# Revit family: plfy-p22_140lmg9_50Hz
name_source: partatom
category: 機械設備
units: mm (PartAtom-declared; Revit-internal decimal feet)

## family parameters
OmniClass タイトル = Split System Air Conditioning Units
OmniClass 番号 = 23.75.10.24.21.27.27
パーツ タイプ = 標準
ロード時にボイドで切り取り = いいえ
丸型コネクタ寸法 = 直径を使用
作業面ベース = いいえ
共有 = いいえ
常に垂直 = はい
部屋計算ポイント = はい

## types (10) — shared parameters
Clearance Back = 500  [stored 1.64042 ft]
Clearance Bottom = 1000  [stored 3.28084 ft]
Clearance Front = 500  [stored 1.64042 ft]
Clearance Left = 1500  [stored 4.92126 ft]
Clearance Right = 1500  [stored 4.92126 ft]
IfcExportAs = IfcUnitaryEquipmentType
IfcExportType = AIRCONDITIONINGUNIT
OmniClassCode = 23-751024212727
URL = https://www.mitsubishielectric.co.jp
Uniclass2015Code = Pr_70_65_03_84
Uniclass2015Title = Split coil remote air cooled condensing units
Uniclass2015Version = Systems v1.9
Width = 650  [stored 2.13255 ft]
ケーブルサイズ = 2 mm
サービススペース = はい
ドレン管径 = 32 mm
ドレン管高さ = 297  [stored 0.974409 ft]
パネルマテリアル = <カテゴリ別>
仕様書バージョン = Version1.0
企業コード = 108420
冷媒ガス管高さ = 235  [stored 0.770997 ft]
冷媒液管高さ = 235  [stored 0.770997 ft]
冷媒管径 = 100 mm
冷媒高低圧ガス管径 = 0 mm
分類コード = 50053003221020
加湿給水管径 = 0 mm
参照している仕様書等のバージョン = 公共建築工事標準仕様書（機械設備工事編）平成31年度版
吊りボルト_H = 167  [stored 0.5479 ft]
吊り位置X = 574  [stored 1.8832 ft]
周波数 = 50 Hz
呼称 = 室内機_カセット形(2方向吹出形)
形式 = カセット形（2方向吹出形）
推奨ブレーカー容量 = 15 A
本体マテリアル = <カテゴリ別>
極数 = 3
機外静圧 = 0.0 Pa
法定耐用年数 = 15
消費電力_加湿器 = 0.00 kW
消費電力_電気ヒーター = 0.00 kW
発停方法 = 付属スイッチ
相 = 1
相_電気ヒーター = 1
積算_科目 = 1 空気調和設備
符号 = ACP_CK2
製品リリース年月 = 2022年9月15日
製品出荷対象 = 国内
製造元 = 三菱電機株式会社
設置方法 = カセット形
設計冷房能力 = 0 kW
設計冷房能力_顕熱 = 0 kW
設計暖房能力 = 0.00 kW
説明 = ビル用マルチエアコン 天井カセット形(2方向吹出)室内機
負荷分類 = 3_ファン類
運転質量 = 0.00 kg
電圧 = 200 V
電圧_電気ヒーター = 0 V
zero-valued in all types: 有効加湿量, 電源_H

## per-type parameters (varying)
- PLFY-P22LMG9: Clearance Top=357  [stored 1.17126 ft]; Depth=770  [stored 2.52625 ft]; Height=290  [stored 0.951444 ft]; MAX風量=570.0 m³/h; MID風量=510.0 m³/h; MID風量2=450.0 m³/h; MIN風量=390.0 m³/h; S_H=364  [stored 1.19423 ft]; 冷媒ガス管径=13 mm; 冷媒ガス管長さ=78  [stored 0.255906 ft]; 冷媒液管径=6 mm; 冷媒液管長さ=67  [stored 0.219816 ft]; 冷媒管径符号=Ac; 冷房能力=2.2 kW; 吊り位置Y=824  [stored 2.70341 ft]; 暖房能力=2.50 kW; 消費電力=0.03 kW; 消費電力_冷房=0.03 kW; 消費電力_暖房=0.03 kW; 製品質量=20.00 kg; 質量=24.00 kg; 電動機出力_送風機=0.05 kW; 音響パワーレベル(dB)=53; 音響パワーレベル（中1）(dB)=52; 音響パワーレベル（中2）(dB)=51; 音響パワーレベル（弱）(dB)=49; 風量=570.0 m³/h; 風量（m3／min）=9.5; 風量（中1）（m3／min）=8.5; 風量（中2）（m3／min）=7.5; 風量（弱）（m3／min）=6.5
- PLFY-P28LMG9: Clearance Top=357  [stored 1.17126 ft]; Depth=770  [stored 2.52625 ft]; Height=290  [stored 0.951444 ft]; MAX風量=570.0 m³/h; MID風量=510.0 m³/h; MID風量2=450.0 m³/h; MIN風量=390.0 m³/h; S_H=364  [stored 1.19423 ft]; 冷媒ガス管径=13 mm; 冷媒ガス管長さ=78  [stored 0.255906 ft]; 冷媒液管径=6 mm; 冷媒液管長さ=67  [stored 0.219816 ft]; 冷媒管径符号=Ac; 冷房能力=2.8 kW; 吊り位置Y=824  [stored 2.70341 ft]; 暖房能力=3.20 kW; 消費電力=0.03 kW; 消費電力_冷房=0.03 kW; 消費電力_暖房=0.03 kW; 製品質量=20.00 kg; 質量=24.00 kg; 電動機出力_送風機=0.05 kW; 音響パワーレベル(dB)=53; 音響パワーレベル（中1）(dB)=52; 音響パワーレベル（中2）(dB)=51; 音響パワーレベル（弱）(dB)=49; 風量=570.0 m³/h; 風量（m3／min）=9.5; 風量（中1）（m3／min）=8.5; 風量（中2）（m3／min）=7.5; 風量（弱）（m3／min）=6.5
- PLFY-P36LMG9: Clearance Top=357  [stored 1.17126 ft]; Depth=770  [stored 2.52625 ft]; Height=290  [stored 0.951444 ft]; MAX風量=600.0 m³/h; MID風量=540.0 m³/h; MID風量2=480.0 m³/h; MIN風量=390.0 m³/h; S_H=364  [stored 1.19423 ft]; 冷媒ガス管径=13 mm; 冷媒ガス管長さ=78  [stored 0.255906 ft]; 冷媒液管径=6 mm; 冷媒液管長さ=67  [stored 0.219816 ft]; 冷媒管径符号=Ac; 冷房能力=3.6 kW; 吊り位置Y=824  [stored 2.70341 ft]; 暖房能力=4.00 kW; 消費電力=0.03 kW; 消費電力_冷房=0.03 kW; 消費電力_暖房=0.03 kW; 製品質量=21.00 kg; 質量=25.20 kg; 電動機出力_送風機=0.05 kW; 音響パワーレベル(dB)=53; 音響パワーレベル（中1）(dB)=52; 音響パワーレベル（中2）(dB)=51; 音響パワーレベル（弱）(dB)=50; 風量=600.0 m³/h; 風量（m3／min）=10; 風量（中1）（m3／min）=9; 風量（中2）（m3／min）=8; 風量（弱）（m3／min）=6.5
- PLFY-P45LMG9: Clearance Top=357  [stored 1.17126 ft]; Depth=770  [stored 2.52625 ft]; Height=290  [stored 0.951444 ft]; MAX風量=630.0 m³/h; MID風量=570.0 m³/h; MID風量2=510.0 m³/h; MIN風量=420.0 m³/h; S_H=364  [stored 1.19423 ft]; 冷媒ガス管径=13 mm; 冷媒ガス管長さ=78  [stored 0.255906 ft]; 冷媒液管径=6 mm; 冷媒液管長さ=67  [stored 0.219816 ft]; 冷媒管径符号=Ac; 冷房能力=4.5 kW; 吊り位置Y=824  [stored 2.70341 ft]; 暖房能力=5.00 kW; 消費電力=0.04 kW; 消費電力_冷房=0.04 kW; 消費電力_暖房=0.04 kW; 製品質量=21.00 kg; 質量=25.20 kg; 電動機出力_送風機=0.05 kW; 音響パワーレベル(dB)=56; 音響パワーレベル（中1）(dB)=55; 音響パワーレベル（中2）(dB)=54; 音響パワーレベル（弱）(dB)=51; 風量=630.0 m³/h; 風量（m3／min）=10.5; 風量（中1）（m3／min）=9.5; 風量（中2）（m3／min）=8.5; 風量（弱）（m3／min）=7
- PLFY-P56LMG9: Clearance Top=357  [stored 1.17126 ft]; Depth=940  [stored 3.08399 ft]; Height=290  [stored 0.951444 ft]; MAX風量=780.0 m³/h; MID風量=720.0 m³/h; MID風量2=660.0 m³/h; MIN風量=540.0 m³/h; S_H=364  [stored 1.19423 ft]; 冷媒ガス管径=13 mm; 冷媒ガス管長さ=78  [stored 0.255906 ft]; 冷媒液管径=6 mm; 冷媒液管長さ=67  [stored 0.219816 ft]; 冷媒管径符号=Ac; 冷房能力=5.6 kW; 吊り位置Y=994; 暖房能力=6.30 kW; 消費電力=0.05 kW; 消費電力_冷房=0.05 kW; 消費電力_暖房=0.05 kW; 製品質量=24.00 kg; 質量=28.80 kg; 電動機出力_送風機=0.05 kW; 音響パワーレベル(dB)=57; 音響パワーレベル（中1）(dB)=56; 音響パワーレベル（中2）(dB)=55; 音響パワーレベル（弱）(dB)=53; 風量=780.0 m³/h; 風量（m3／min）=13; 風量（中1）（m3／min）=12; 風量（中2）（m3／min）=11; 風量（弱）（m3／min）=9
- PLFY-P71LMG9: Clearance Top=357  [stored 1.17126 ft]; Depth=940  [stored 3.08399 ft]; Height=290  [stored 0.951444 ft]; MAX風量=990.0 m³/h; MID風量=900.0 m³/h; MID風量2=750.0 m³/h; MIN風量=630.0 m³/h; S_H=364  [stored 1.19423 ft]; 冷媒ガス管径=16 mm; 冷媒ガス管長さ=78  [stored 0.255906 ft]; 冷媒液管径=10 mm; 冷媒液管長さ=67  [stored 0.219816 ft]; 冷媒管径符号=Bd; 冷房能力=7.1 kW; 吊り位置Y=994; 暖房能力=8.00 kW; 消費電力=0.07 kW; 消費電力_冷房=0.07 kW; 消費電力_暖房=0.07 kW; 製品質量=26.00 kg; 質量=31.20 kg; 電動機出力_送風機=0.05 kW; 音響パワーレベル(dB)=60; 音響パワーレベル（中1）(dB)=59; 音響パワーレベル（中2）(dB)=58; 音響パワーレベル（弱）(dB)=55; 風量=990.0 m³/h; 風量（m3／min）=16.5; 風量（中1）（m3／min）=15; 風量（中2）（m3／min）=12.5; 風量（弱）（m3／min）=10.5
- PLFY-P80LMG9: Clearance Top=398  [stored 1.30577 ft]; Depth=1440  [stored 4.72441 ft]; Height=331  [stored 1.08596 ft]; MAX風量=1140.0 m³/h; MID風量=990.0 m³/h; MID風量2=900.0 m³/h; MIN風量=810.0 m³/h; S_H=405  [stored 1.32874 ft]; 冷媒ガス管径=16 mm; 冷媒ガス管長さ=83  [stored 0.27231 ft]; 冷媒液管径=10 mm; 冷媒液管長さ=71  [stored 0.23294 ft]; 冷媒管径符号=Bd; 冷房能力=8 kW; 吊り位置Y=1494  [stored 4.90157 ft]; 暖房能力=9.00 kW; 消費電力=0.06 kW; 消費電力_冷房=0.06 kW; 消費電力_暖房=0.06 kW; 製品質量=41.00 kg; 質量=49.20 kg; 電動機出力_送風機=0.10 kW; 音響パワーレベル(dB)=60; 音響パワーレベル（中1）(dB)=59; 音響パワーレベル（中2）(dB)=58; 音響パワーレベル（弱）(dB)=56; 風量=1140.0 m³/h; 風量（m3／min）=19; 風量（中1）（m3／min）=16.5; 風量（中2）（m3／min）=15; 風量（弱）（m3／min）=13.5
- PLFY-P90LMG9: Clearance Top=398  [stored 1.30577 ft]; Depth=1440  [stored 4.72441 ft]; Height=331  [stored 1.08596 ft]; MAX風量=1350.0 m³/h; MID風量=1200.0 m³/h; MID風量2=1080.0 m³/h; MIN風量=930.0 m³/h; S_H=405  [stored 1.32874 ft]; 冷媒ガス管径=16 mm; 冷媒ガス管長さ=83  [stored 0.27231 ft]; 冷媒液管径=10 mm; 冷媒液管長さ=71  [stored 0.23294 ft]; 冷媒管径符号=Bd; 冷房能力=9 kW; 吊り位置Y=1494  [stored 4.90157 ft]; 暖房能力=10.00 kW; 消費電力=0.08 kW; 消費電力_冷房=0.08 kW; 消費電力_暖房=0.08 kW; 製品質量=41.00 kg; 質量=49.20 kg; 電動機出力_送風機=0.10 kW; 音響パワーレベル(dB)=61; 音響パワーレベル（中1）(dB)=60; 音響パワーレベル（中2）(dB)=59; 音響パワーレベル（弱）(dB)=57; 風量=1350.0 m³/h; 風量（m3／min）=22.5; 風量（中1）（m3／min）=20; 風量（中2）（m3／min）=18; 風量（弱）（m3／min）=15.5
- PLFY-P112LMG9: Clearance Top=398  [stored 1.30577 ft]; Depth=1440  [stored 4.72441 ft]; Height=331  [stored 1.08596 ft]; MAX風量=1560.0 m³/h; MID風量=1410.0 m³/h; MID風量2=1200.0 m³/h; MIN風量=1080.0 m³/h; S_H=405  [stored 1.32874 ft]; 冷媒ガス管径=16 mm; 冷媒ガス管長さ=83  [stored 0.27231 ft]; 冷媒液管径=10 mm; 冷媒液管長さ=71  [stored 0.23294 ft]; 冷媒管径符号=Bd; 冷房能力=11.2 kW; 吊り位置Y=1494  [stored 4.90157 ft]; 暖房能力=12.50 kW; 消費電力=0.10 kW; 消費電力_冷房=0.10 kW; 消費電力_暖房=0.10 kW; 製品質量=45.00 kg; 質量=54.00 kg; 電動機出力_送風機=0.10 kW; 音響パワーレベル(dB)=63; 音響パワーレベル（中1）(dB)=62; 音響パワーレベル（中2）(dB)=61; 音響パワーレベル（弱）(dB)=59; 風量=1560.0 m³/h; 風量（m3／min）=26; 風量（中1）（m3／min）=23.5; 風量（中2）（m3／min）=20; 風量（弱）（m3／min）=18
- PLFY-P140LMG9: Clearance Top=398  [stored 1.30577 ft]; Depth=1440  [stored 4.72441 ft]; Height=331  [stored 1.08596 ft]; MAX風量=1890.0 m³/h; MID風量=1710.0 m³/h; MID風量2=1590.0 m³/h; MIN風量=1380.0 m³/h; S_H=405  [stored 1.32874 ft]; 冷媒ガス管径=16 mm; 冷媒ガス管長さ=83  [stored 0.27231 ft]; 冷媒液管径=10 mm; 冷媒液管長さ=71  [stored 0.23294 ft]; 冷媒管径符号=Bd; 冷房能力=14 kW; 吊り位置Y=1494  [stored 4.90157 ft]; 暖房能力=16.00 kW; 消費電力=0.20 kW; 消費電力_冷房=0.20 kW; 消費電力_暖房=0.20 kW; 製品質量=47.00 kg; 質量=56.40 kg; 電動機出力_送風機=0.24 kW; 音響パワーレベル(dB)=69; 音響パワーレベル（中1）(dB)=67; 音響パワーレベル（中2）(dB)=64; 音響パワーレベル（弱）(dB)=63; 風量=1890.0 m³/h; 風量（m3／min）=31.5; 風量（中1）（m3／min）=28.5; 風量（中2）（m3／min）=26.5; 風量（弱）（m3／min）=23

note: column(s) folded — value = type name in every type: モデル

note: [stored X ft] marks values corroborated as IEEE doubles in the binary element streams (Revit-internal decimal feet)

## geometry (parser evidence)
native form markers: Blend x8
no freeform markers — native parametric forms only
